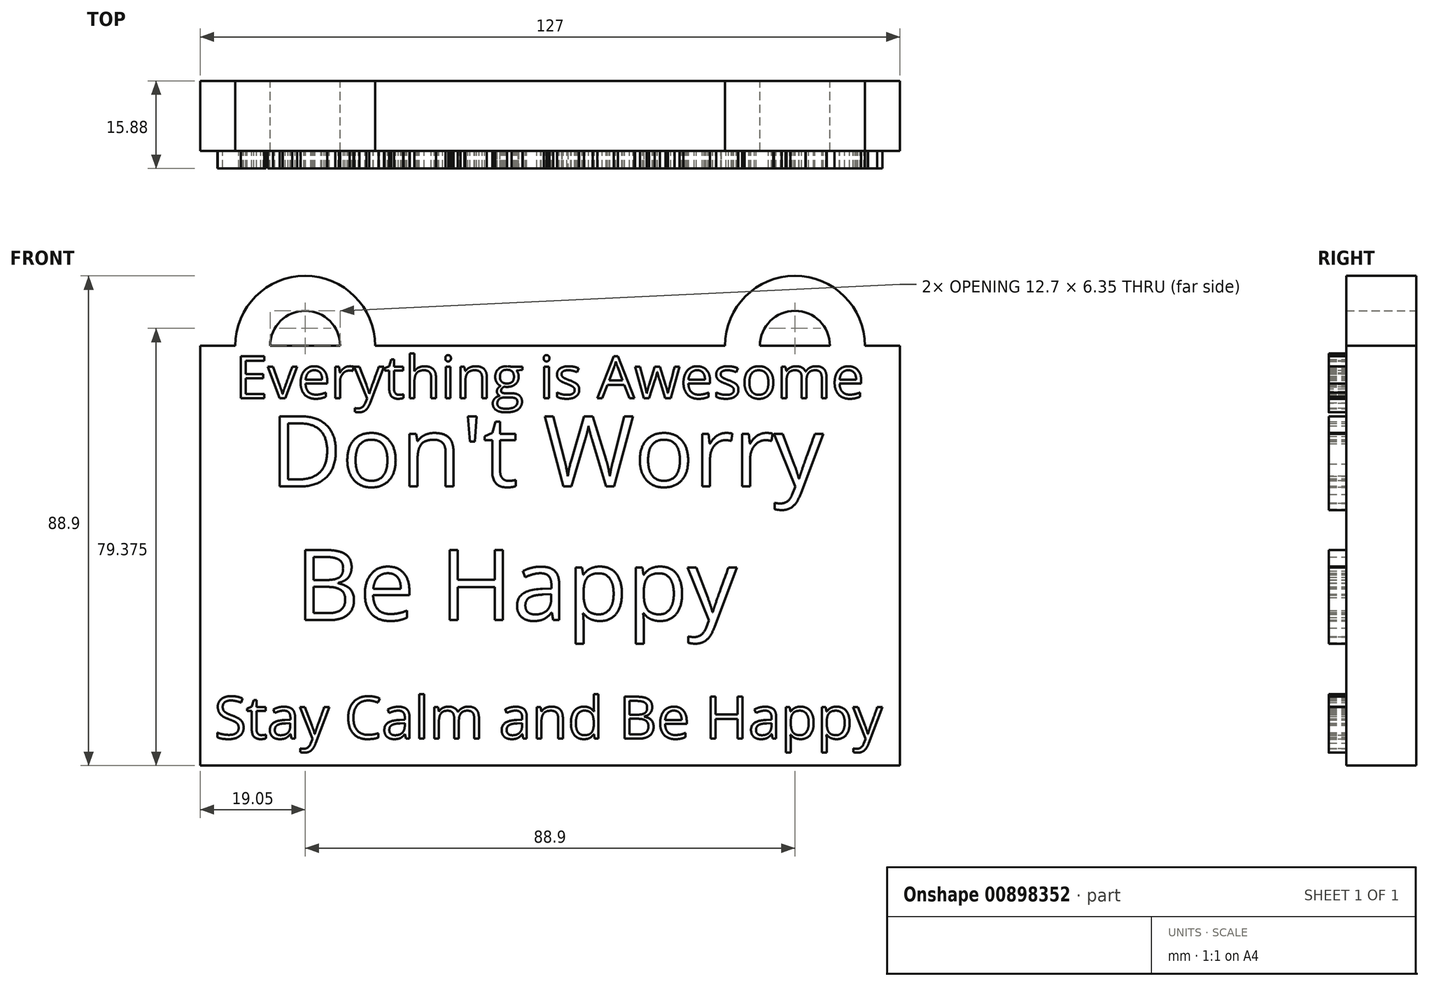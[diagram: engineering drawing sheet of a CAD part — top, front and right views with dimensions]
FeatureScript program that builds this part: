
annotation { "Feature Type Name" : "Feature", "Feature Type Description" : "" }
export const myFeature = defineFeature(function(context is Context, id is Id, definition is map)
    precondition{}
    {
        {
            var Q0;
            Q0=qCreatedBy(makeId("Front.planeOp"),FACE);
            var sketch = newSketch(context, id + "F0", { "sketchPlane" : qUnion([Q0])});
            skLineSegment(sketch, "E0.bottom", {"start": v(63.5, 38.1) * mm, "end": v(-63.5, 38.1) * mm});
            skLineSegment(sketch, "E0.top", {"start": v(63.5, -38.1) * mm, "end": v(-63.5, -38.1) * mm});
            skLineSegment(sketch, "E0.left", {"start": v(63.5, 38.1) * mm, "end": v(63.5, -38.1) * mm});
            skLineSegment(sketch, "E0.right", {"start": v(-63.5, 38.1) * mm, "end": v(-63.5, -38.1) * mm});
            skPoint(sketch, "E0.middle", {"position": v(0, 0) * mm});
            skArc(sketch, "E1", {"start": v(-38.1, 38.1) * mm, "mid": v(-44.45, 44.45) * mm, "end": v(-50.8, 38.1) * mm});
            skArc(sketch, "E2", {"start": v(50.8, 38.1) * mm, "mid": v(44.45, 44.45) * mm, "end": v(38.1, 38.1) * mm});
            skArc(sketch, "E3", {"start": v(-31.75, 38.1) * mm, "mid": v(-44.45, 50.8) * mm, "end": v(-57.15, 38.1) * mm});
            skArc(sketch, "E4", {"start": v(57.15, 38.1) * mm, "mid": v(44.45, 50.8) * mm, "end": v(31.75, 38.1) * mm});
            skLineSegment(sketch, "E5", {"start": v(-57.15, 38.1) * mm, "end": v(-50.8, 38.1) * mm});
            skLineSegment(sketch, "E6", {"start": v(-38.1, 38.1) * mm, "end": v(-31.75, 38.1) * mm});
            skLineSegment(sketch, "E7", {"start": v(31.75, 38.1) * mm, "end": v(38.1, 38.1) * mm});
            skLineSegment(sketch, "E8", {"start": v(50.8, 38.1) * mm, "end": v(57.15, 38.1) * mm});
            skSolve(sketch);
        }
        {
            var Q0;
            {var subQ7=sQuery(id+"F0.wireOp",EDGE,"E1");var subQ12=sQuery(id+"F0.wireOp",EDGE,"E2");Q0=qUnion([makeQuery(id+"F0.imprint","IMPRINT",FACE,{"disambiguationData":[TD([[makeQuery(id+"F0.imprint","IMPRINT",EDGE,{"derivedFrom":subQ7}),-1.0]])]}),makeQuery(id+"F0.imprint","IMPRINT",FACE,{"disambiguationData":[TD([[makeQuery(id+"F0.imprint","IMPRINT",EDGE,{"derivedFrom":subQ12}),-1.0]])]}),makeQuery(id+"F0.imprint","IMPRINT",FACE,{"disambiguationData":[TD([[makeQuery(id+"F0.imprint","IMPRINT",EDGE,{"derivedFrom":sQuery(id+"F0.wireOp",EDGE,"E0.top")}),-1.0]])]})]);}
            extrude(context, id + "F1", {"entities" : qUnion([Q0]), "depth" : 12.7 * mm, "offsetDistance" : 25.4 * mm});
        }
        {
            var Q0;
            Q0=makeQuery(id+"F1.opExtrude","CAP_FACE",FACE,{"disambiguationData":[OSD([sQuery(id+"F0.wireOp",EDGE,"E0.bottom"),sQuery(id+"F0.wireOp",EDGE,"E0.top"),sQuery(id+"F0.wireOp",EDGE,"E0.left"),sQuery(id+"F0.wireOp",EDGE,"E0.right"),sQuery(id+"F0.wireOp",EDGE,"E1"),sQuery(id+"F0.wireOp",EDGE,"E2"),sQuery(id+"F0.wireOp",EDGE,"E3"),sQuery(id+"F0.wireOp",EDGE,"E4")])],"isStart":false});
            var sketch = newSketch(context, id + "F2", { "sketchPlane" : qUnion([Q0])});
            skText(sketch, "E9", { "text": "Don\'t Worry\n Be Happy", "fontName": "OpenSans-Regular.ttf"});
            skText(sketch, "E10", { "text": "Stay Calm and Be Happy", "fontName": "OpenSans-Regular.ttf"});
            skLineSegment(sketch, "E11", {"start": v(-50.8, 38.1) * mm, "end": v(-50.8, -38.1) * mm, "construction": true});
            skLineSegment(sketch, "E12", {"start": v(50.8, 38.1) * mm, "end": v(50.8, -38.1) * mm, "construction": true});
            skText(sketch, "E13", { "text": "Everything is Awesome", "fontName": "OpenSans-Regular.ttf"});
            const initialGuessF2  = {"E9": [-0.0508, 0.01256, 1, 0, 0.01284], "E10": [-0.06096, -0.03321, 1, 0, 0.00767], "E13": [-0.05715, 0.02858, 1, 0, 0.00768]};
            skSetInitialGuess(sketch, initialGuessF2);
            skSolve(sketch);
        }
        {
            var Q0;
            Q0 = qSketchRegion(id + "F2", true);
            extrude(context, id + "F3", {"entities" : qUnion([Q0]), "operationType" : NewBodyOperationType.ADD, "depth" : 3.17 * mm, "offsetDistance" : 25.4 * mm});
        }
    });
